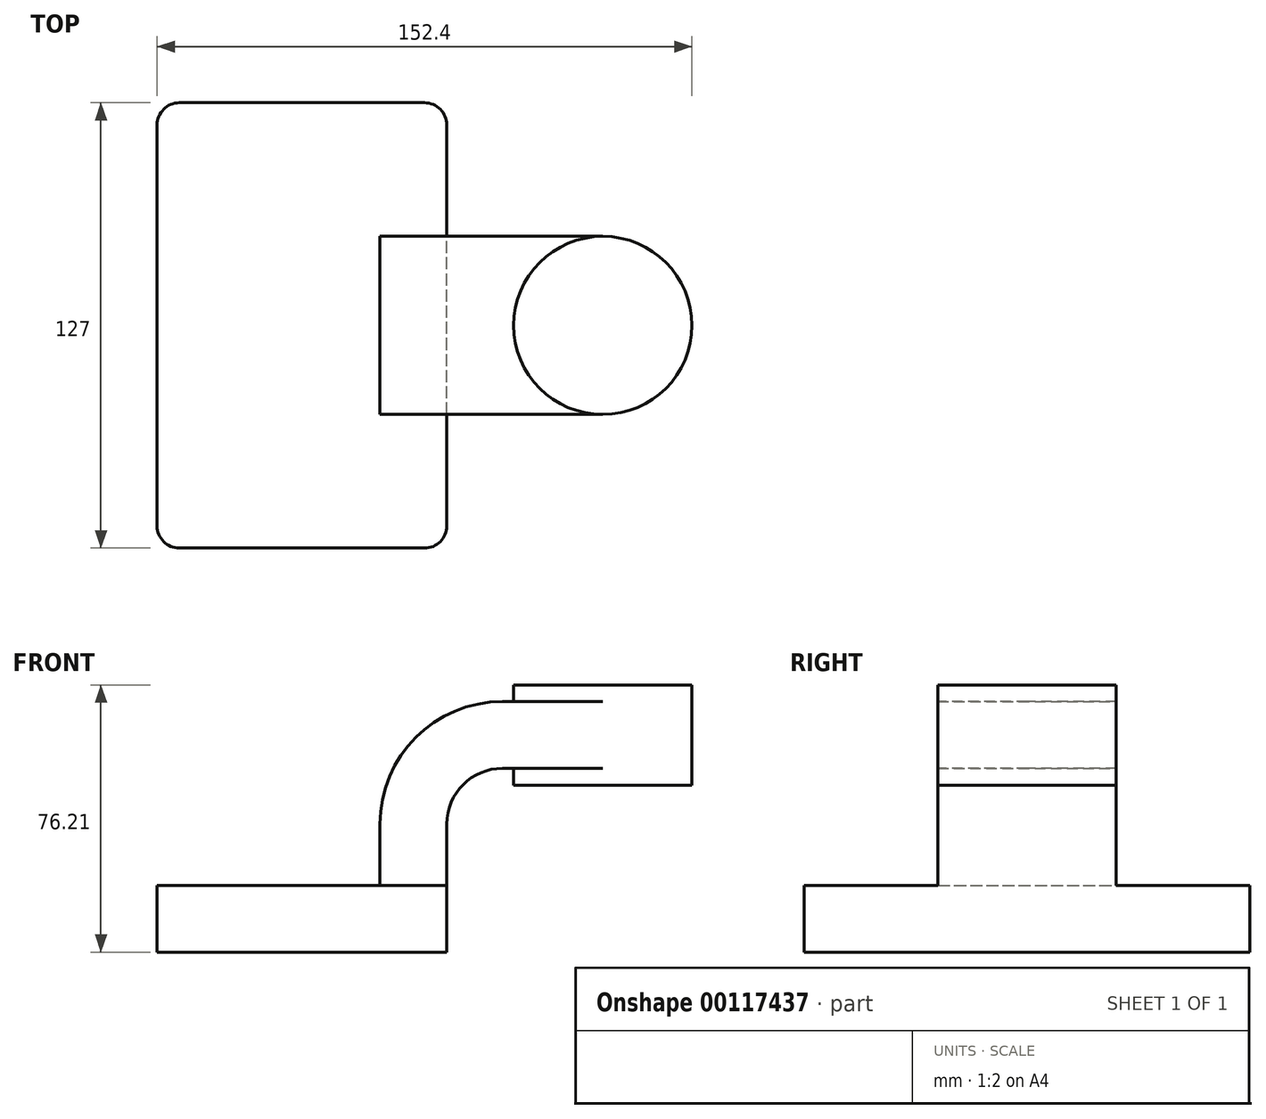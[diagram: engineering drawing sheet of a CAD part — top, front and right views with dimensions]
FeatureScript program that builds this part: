
annotation { "Feature Type Name" : "Feature", "Feature Type Description" : "" }
export const myFeature = defineFeature(function(context is Context, id is Id, definition is map)
    precondition{}
    {
        {
            var Q0;
            Q0=qCreatedBy(makeId("Front.planeOp"),FACE);
            var sketch = newSketch(context, id + "F0", { "sketchPlane" : qUnion([Q0])});
            skLineSegment(sketch, "E0.bottom", {"start": v(41.27, 9.53) * mm, "end": v(-41.28, 9.53) * mm});
            skLineSegment(sketch, "E0.top", {"start": v(41.28, -9.52) * mm, "end": v(-41.27, -9.52) * mm});
            skLineSegment(sketch, "E0.left", {"start": v(41.27, 9.53) * mm, "end": v(41.28, -9.52) * mm});
            skLineSegment(sketch, "E0.right", {"start": v(-41.28, 9.53) * mm, "end": v(-41.27, -9.52) * mm});
            skPoint(sketch, "E0.middle", {"position": v(0, 0) * mm});
            skLineSegment(sketch, "E1.bottom", {"start": v(111.12, 38.1) * mm, "end": v(60.33, 38.1) * mm});
            skLineSegment(sketch, "E1.top", {"start": v(111.12, 66.68) * mm, "end": v(60.32, 66.68) * mm});
            skLineSegment(sketch, "E1.left", {"start": v(111.12, 38.1) * mm, "end": v(111.12, 66.68) * mm});
            skLineSegment(sketch, "E1.right", {"start": v(60.32, 38.1) * mm, "end": v(60.32, 66.68) * mm});
            skPoint(sketch, "E1.middle", {"position": v(85.72, 52.39) * mm});
            skLineSegment(sketch, "E2", {"start": v(41.27, 9.53) * mm, "end": v(41.27, 27) * mm});
            skArc(sketch, "E3", {"start": v(41.27, 27) * mm, "mid": v(45.92, 38.23) * mm, "end": v(57.15, 42.88) * mm});
            skLineSegment(sketch, "E4", {"start": v(57.15, 42.88) * mm, "end": v(85.72, 42.88) * mm});
            skLineSegment(sketch, "E5.0", {"start": v(57.15, 61.93) * mm, "end": v(85.72, 61.93) * mm});
            skArc(sketch, "E5.1", {"start": v(22.22, 27) * mm, "mid": v(32.45, 51.7) * mm, "end": v(57.15, 61.93) * mm});
            skLineSegment(sketch, "E5.2", {"start": v(22.22, 9.53) * mm, "end": v(22.22, 27) * mm});
            skLineSegment(sketch, "E6", {"start": v(85.72, 38.1) * mm, "end": v(85.72, 66.68) * mm});
            skFitSpline(sketch, "E7", {"points": [v(-41.28, 9.53) * mm, v(57.15, 61.93) * mm], "startDerivative": vector(2.3, 117.6) * mm, "endDerivative": vector(147.43, -0.1) * mm});
            skSolve(sketch);
        }
        {
            var Q0;
            Q0=makeQuery(id+"F0.imprint","IMPRINT",FACE,{"disambiguationData":[TD([[makeQuery(id+"F0.imprint","IMPRINT",EDGE,{"derivedFrom":sQuery(id+"F0.wireOp",EDGE,"E0.top")}),-1.0]])]});
            extrude(context, id + "F1", {"entities" : qUnion([Q0]), "endBound" : BoundingType.SYMMETRIC, "depth" : 127 * mm});
        }
        {
            var Q0;
            {var subQ1=sQuery(id+"F0.wireOp",EDGE,"E2");Q0=makeQuery(id+"F0.imprint","IMPRINT",FACE,{"disambiguationData":[TD([[makeQuery(id+"F0.imprint","IMPRINT",EDGE,{"derivedFrom":subQ1}),1.0]])]});}
            var Q1;
            {var subQ0=sQuery(id+"F0.wireOp",EDGE,"E4");var subQ1=sQuery(id+"F0.wireOp",EDGE,"E1.right");var subQ2=makeQuery(id+"F0.imprint","INTERSECT",VERTEX,{"derivedFrom":[subQ1,subQ0]});Q1=makeQuery(id+"F0.imprint","IMPRINT",FACE,{"disambiguationData":[TD([[makeQuery(id+"F0.imprint","IMPRINT",EDGE,{"disambiguationData":[TD([[subQ2,-1.0]])],"derivedFrom":subQ1}),-1.0]])]});}
            extrude(context, id + "F2", {"entities" : qUnion([Q0, Q1]), "operationType" : NewBodyOperationType.ADD, "endBound" : BoundingType.SYMMETRIC, "depth" : 50.8 * mm});
        }
        {
            var Q0;
            Q0=makeQuery(id+"F0.imprint","IMPRINT",FACE,{"disambiguationData":[TD([[makeQuery(id+"F0.imprint","IMPRINT",EDGE,{"derivedFrom":sQuery(id+"F0.wireOp",EDGE,"E5.1")}),1.0]])]});
            extrude(context, id + "F3", {"entities" : qUnion([Q0]), "operationType" : NewBodyOperationType.ADD, "endBound" : BoundingType.SYMMETRIC, "depth" : 15.88 * mm});
        }
        {
            var Q0;
            {var subQ0=sQuery(id+"F0.wireOp",EDGE,"E1.left");Q0=makeQuery(id+"F0.imprint","IMPRINT",FACE,{"disambiguationData":[TD([[makeQuery(id+"F0.imprint","IMPRINT",EDGE,{"derivedFrom":subQ0}),1.0]])]});}
            var Q1;
            Q1=sQuery(id+"F0.wireOp",EDGE,"E6");
            revolve(context, id + "F4", {"operationType" : NewBodyOperationType.ADD, "entities" : qUnion([Q0]), "axis" : qUnion([Q1]), "revolveType" : RevolveType.FULL});
        }
        {
            var Q0;
            Q0=makeQuery(id+"F1.opExtrude","CAP_EDGE",EDGE,{"disambiguationData":[OSD([sQuery(id+"F0.wireOp",EDGE,"E0.right")])],"isStart":false});
            var Q1;
            Q1=makeQuery(id+"F1.opExtrude","CAP_EDGE",EDGE,{"disambiguationData":[OSD([sQuery(id+"F0.wireOp",EDGE,"E0.left")])],"isStart":false});
            var Q2;
            Q2=makeQuery(id+"F1.opExtrude","CAP_EDGE",EDGE,{"disambiguationData":[OSD([sQuery(id+"F0.wireOp",EDGE,"E0.left")])],"isStart":true});
            var Q3;
            Q3=makeQuery(id+"F1.opExtrude","CAP_EDGE",EDGE,{"disambiguationData":[OSD([sQuery(id+"F0.wireOp",EDGE,"E0.right")])],"isStart":true});
            fillet(context, id + "F5", {"entities" : qUnion([Q0, Q1, Q2, Q3]), "radius" : 6.35 * mm, "tangentPropagation" : true, "allowEdgeOverflow" : false});
        }
    });
